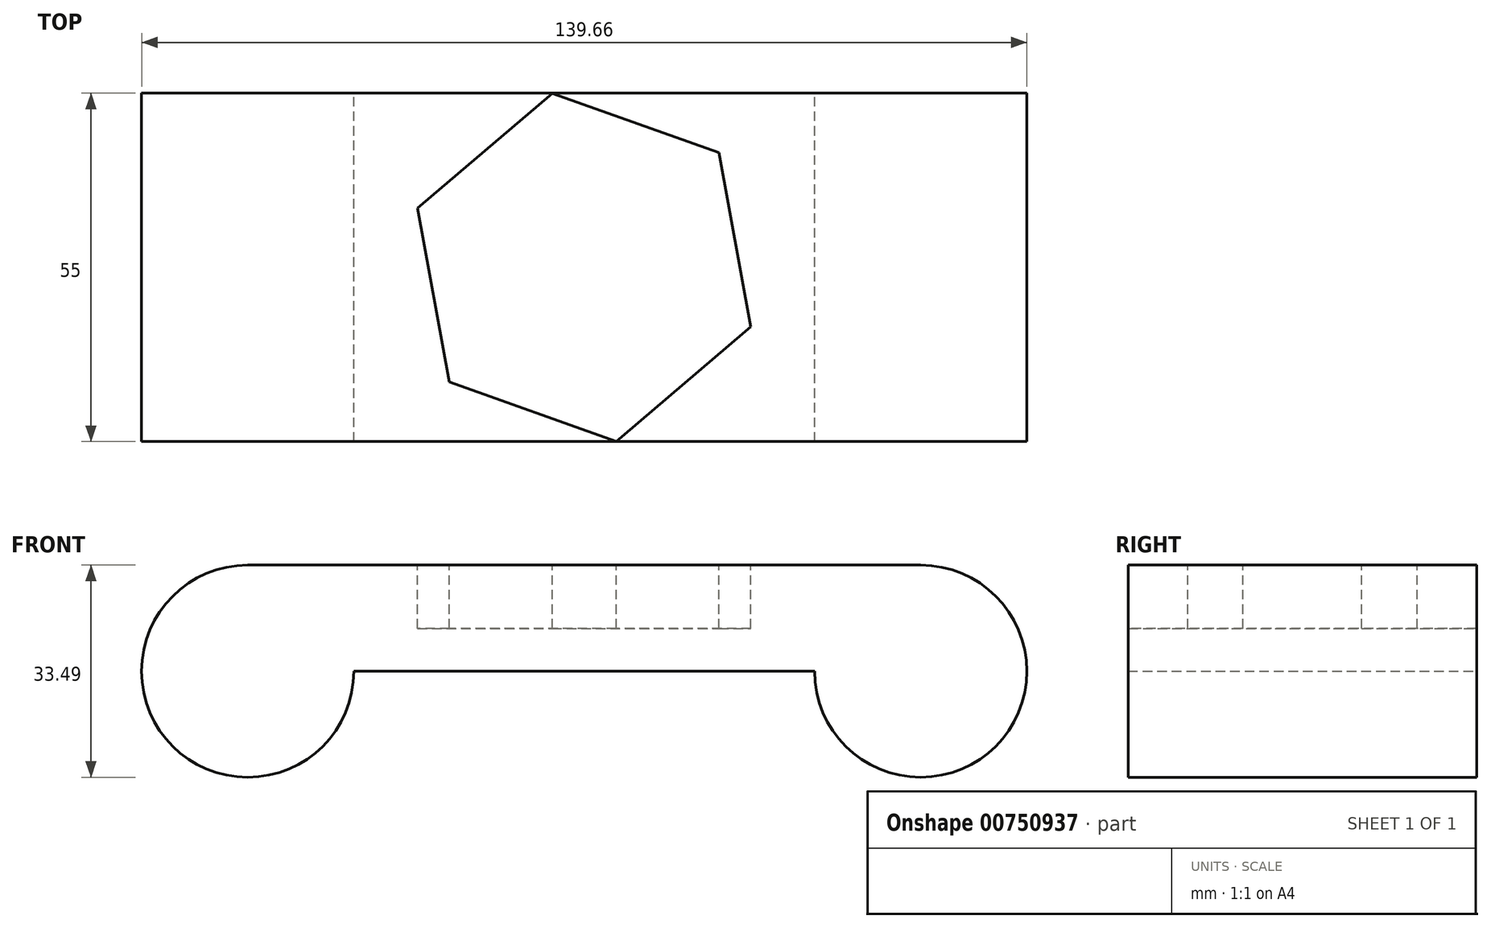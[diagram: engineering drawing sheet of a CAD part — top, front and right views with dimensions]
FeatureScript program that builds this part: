
annotation { "Feature Type Name" : "Feature", "Feature Type Description" : "" }
export const myFeature = defineFeature(function(context is Context, id is Id, definition is map)
    precondition{}
    {
        {
            var Q0;
            Q0=qCreatedBy(makeId("Front.planeOp"),FACE);
            var sketch = newSketch(context, id + "F0", { "sketchPlane" : qUnion([Q0])});
            skLineSegment(sketch, "E0.bottom", {"start": v(53.09, 8.37) * mm, "end": v(-53.09, 8.37) * mm});
            skLineSegment(sketch, "E0.top", {"start": v(53.09, -8.37) * mm, "end": v(-53.09, -8.37) * mm});
            skLineSegment(sketch, "E0.left", {"start": v(53.09, 8.37) * mm, "end": v(53.09, -8.37) * mm});
            skLineSegment(sketch, "E0.right", {"start": v(-53.09, 8.37) * mm, "end": v(-53.09, -8.37) * mm});
            skPoint(sketch, "E0.middle", {"position": v(0, 0) * mm});
            skCircle(sketch, "E1", {"center": v(-53.09, -8.37) * mm, "radius": 16.74 * mm});
            skCircle(sketch, "E2", {"center": v(53.09, -8.37) * mm, "radius": 16.74 * mm});
            skSolve(sketch);
        }
        {
            var Q0;
            {var subQ0=sQuery(id+"F0.wireOp",EDGE,"E0.left");Q0=makeQuery(id+"F0.imprint","IMPRINT",FACE,{"disambiguationData":[TD([[makeQuery(id+"F0.imprint","IMPRINT",EDGE,{"derivedFrom":subQ0}),1.0]])]});}
            var Q1;
            {var subQ0=sQuery(id+"F0.wireOp",EDGE,"E0.bottom");Q1=makeQuery(id+"F0.imprint","IMPRINT",FACE,{"disambiguationData":[TD([[makeQuery(id+"F0.imprint","IMPRINT",EDGE,{"derivedFrom":subQ0}),1.0]])]});}
            var Q2;
            {var subQ0=sQuery(id+"F0.wireOp",EDGE,"E0.right");Q2=makeQuery(id+"F0.imprint","IMPRINT",FACE,{"disambiguationData":[TD([[makeQuery(id+"F0.imprint","IMPRINT",EDGE,{"derivedFrom":subQ0}),-1.0]])]});}
            var Q3;
            {var subQ0=sQuery(id+"F0.wireOp",EDGE,"E0.left");Q3=makeQuery(id+"F0.imprint","IMPRINT",FACE,{"disambiguationData":[TD([[makeQuery(id+"F0.imprint","IMPRINT",EDGE,{"derivedFrom":subQ0}),-1.0]])]});}
            var Q4;
            {var subQ0=sQuery(id+"F0.wireOp",EDGE,"E0.right");Q4=makeQuery(id+"F0.imprint","IMPRINT",FACE,{"disambiguationData":[TD([[makeQuery(id+"F0.imprint","IMPRINT",EDGE,{"derivedFrom":subQ0}),1.0]])]});}
            extrude(context, id + "F1", {"entities" : qUnion([Q0, Q1, Q2, Q3, Q4]), "endBound" : BoundingType.SYMMETRIC, "depth" : 55 * mm, "offsetDistance" : 25 * mm});
        }
        {
            var Q0;
            Q0=makeQuery(id+"F1.opExtrude","SWEPT_FACE",FACE,{"disambiguationData":[OSD([sQuery(id+"F0.wireOp",EDGE,"E0.bottom")])]});
            var sketch = newSketch(context, id + "F2", { "sketchPlane" : qUnion([Q0])});
            skCircle(sketch, "E3.cCircle", {"center": v(0, 0) * mm, "radius": 27.92 * mm, "construction": true});
            skLineSegment(sketch, "E3.0", {"start": v(21.26, 18.1) * mm, "end": v(26.3, -9.36) * mm});
            skLineSegment(sketch, "E3.1", {"start": v(26.3, -9.36) * mm, "end": v(5.04, -27.46) * mm});
            skLineSegment(sketch, "E3.2", {"start": v(5.04, -27.46) * mm, "end": v(-21.26, -18.1) * mm});
            skLineSegment(sketch, "E3.3", {"start": v(-21.26, -18.1) * mm, "end": v(-26.3, 9.36) * mm});
            skLineSegment(sketch, "E3.4", {"start": v(-26.3, 9.36) * mm, "end": v(-5.04, 27.46) * mm});
            skLineSegment(sketch, "E3.5", {"start": v(-5.04, 27.46) * mm, "end": v(21.26, 18.1) * mm});
            skSolve(sketch);
        }
        {
            var Q0;
            Q0=makeQuery(id+"F2.imprint","IMPRINT",FACE,{"disambiguationData":[TD([[makeQuery(id+"F2.imprint","IMPRINT",EDGE,{"derivedFrom":sQuery(id+"F2.wireOp",EDGE,"E3.0")}),-1.0]])]});
            extrude(context, id + "F3", {"entities" : qUnion([Q0]), "operationType" : NewBodyOperationType.REMOVE, "oppositeDirection" : true, "depth" : 10 * mm, "offsetDistance" : 25 * mm});
        }
    });
